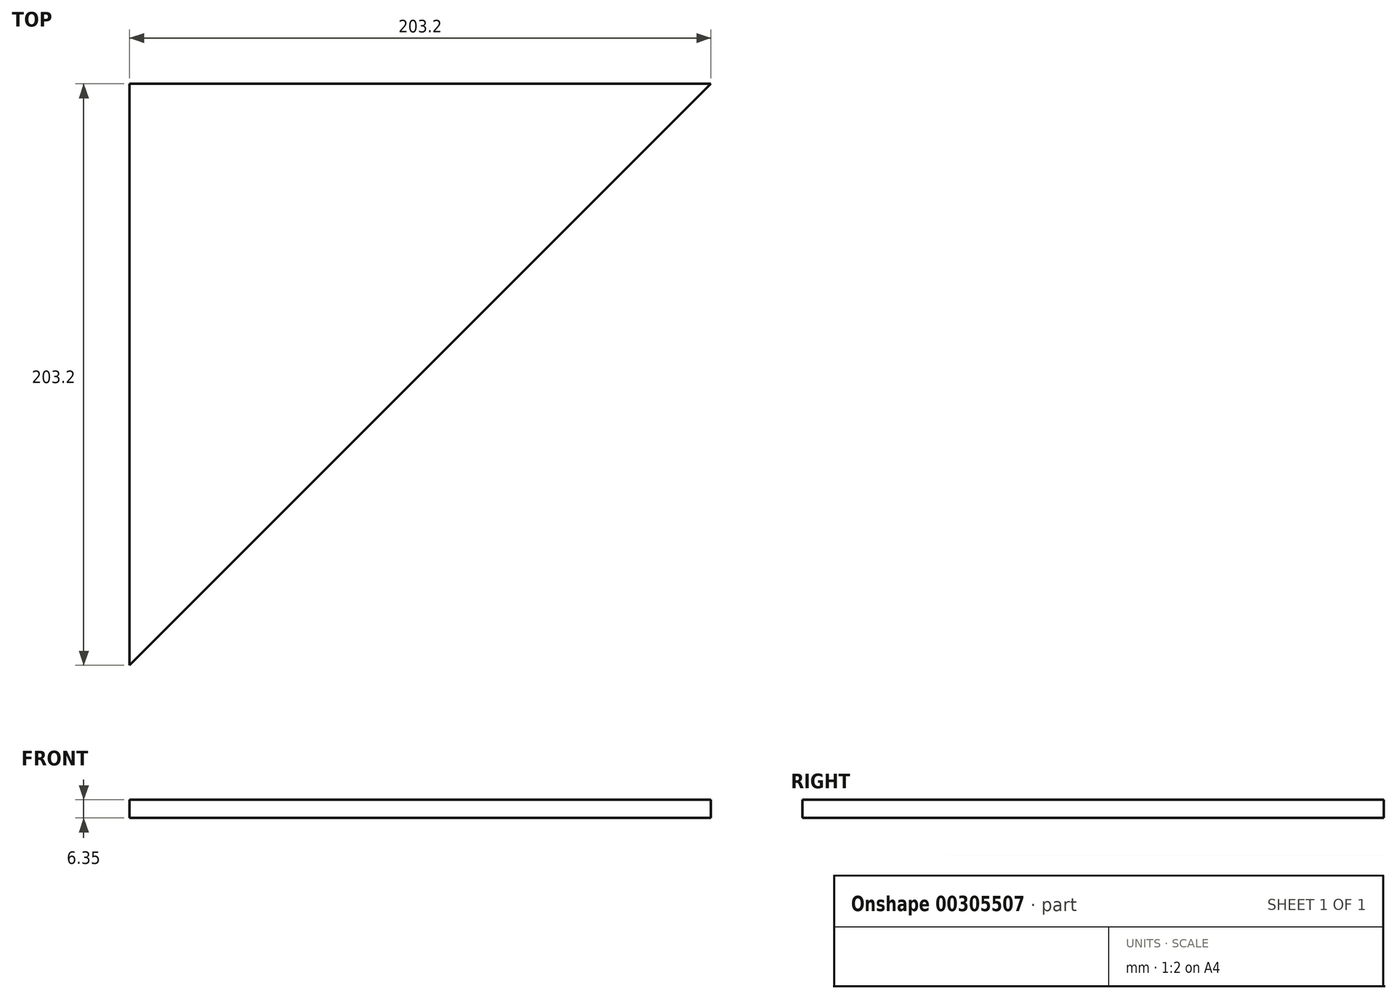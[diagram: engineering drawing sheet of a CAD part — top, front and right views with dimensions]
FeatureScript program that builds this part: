
annotation { "Feature Type Name" : "Feature", "Feature Type Description" : "" }
export const myFeature = defineFeature(function(context is Context, id is Id, definition is map)
    precondition{}
    {
        {
            var Q0;
            Q0=qCreatedBy(makeId("Top.planeOp"),FACE);
            var sketch = newSketch(context, id + "F0", { "sketchPlane" : qUnion([Q0])});
            skLineSegment(sketch, "E0.bottom", {"start": v(-92.89, 74.85) * mm, "end": v(110.31, 74.85) * mm});
            skLineSegment(sketch, "E0.left", {"start": v(-92.89, 74.85) * mm, "end": v(-92.89, -128.35) * mm});
            skLineSegment(sketch, "E1", {"start": v(-92.89, -128.35) * mm, "end": v(110.31, 74.85) * mm});
            skSolve(sketch);
        }
        {
            var Q0;
            Q0=makeQuery(id+"F0.imprint","IMPRINT",FACE,{"disambiguationData":[TD([[makeQuery(id+"F0.imprint","IMPRINT",EDGE,{"derivedFrom":sQuery(id+"F0.wireOp",EDGE,"E0.bottom")}),-1.0]])]});
            extrude(context, id + "F1", {"entities" : qUnion([Q0]), "depth" : 6.35 * mm});
        }
    });
